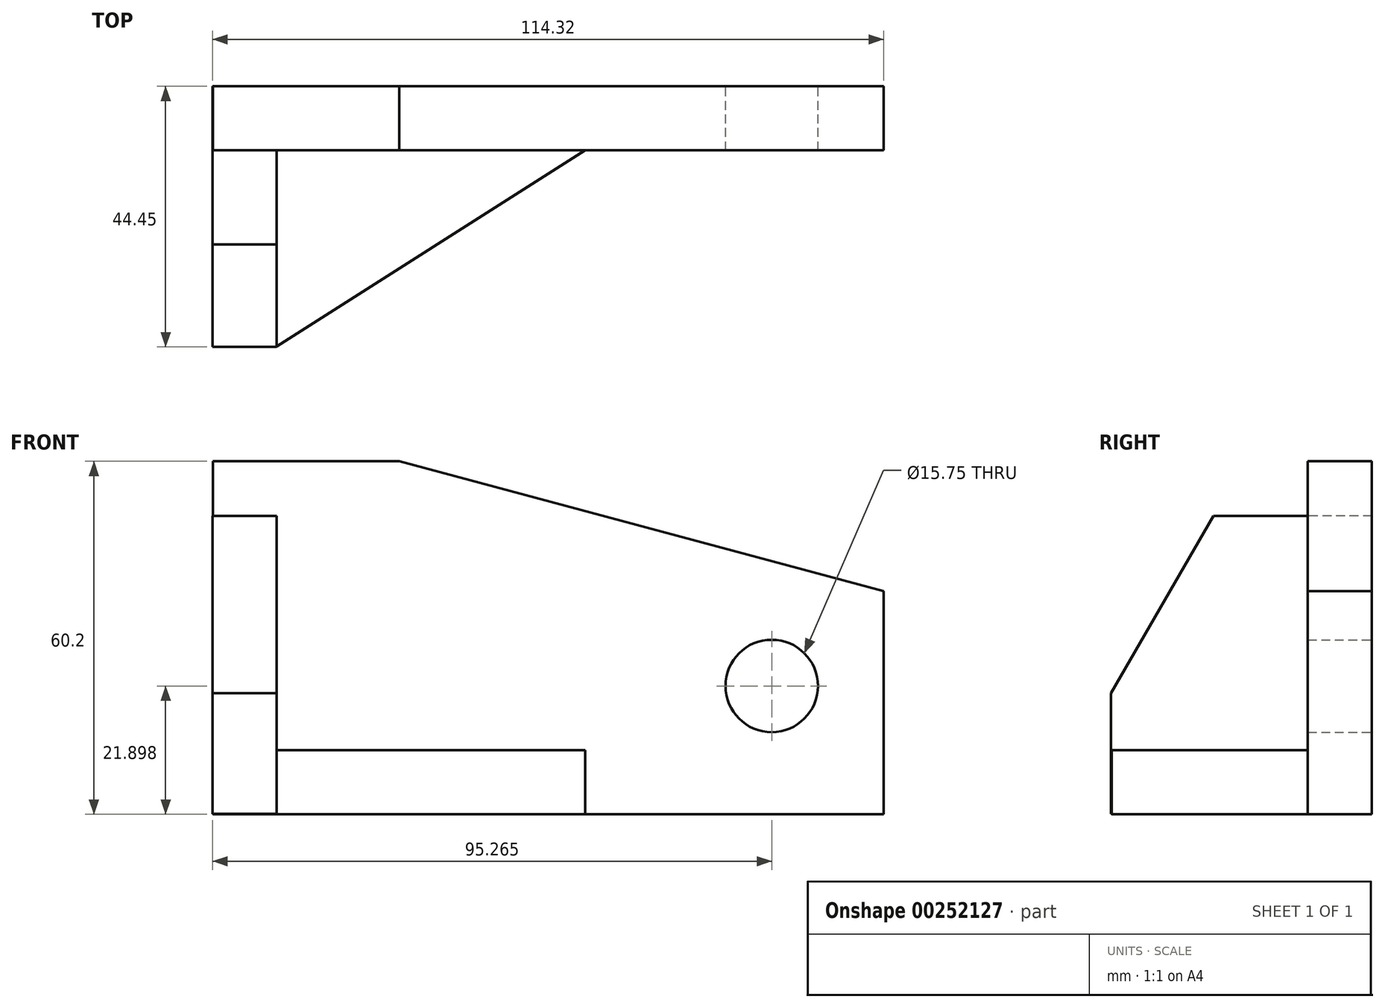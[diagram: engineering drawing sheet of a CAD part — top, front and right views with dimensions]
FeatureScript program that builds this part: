
annotation { "Feature Type Name" : "Feature", "Feature Type Description" : "" }
export const myFeature = defineFeature(function(context is Context, id is Id, definition is map)
    precondition{}
    {
        {
            var Q0;
            Q0=qCreatedBy(makeId("Front.planeOp"),FACE);
            var sketch = newSketch(context, id + "F0", { "sketchPlane" : qUnion([Q0])});
            skLineSegment(sketch, "E0", {"start": v(-57.08, 27.38) * mm, "end": v(-25.33, 27.38) * mm});
            skLineSegment(sketch, "E1", {"start": v(-57.08, 27.38) * mm, "end": v(-57.08, 0) * mm});
            skLineSegment(sketch, "E2", {"start": v(-57.08, 0) * mm, "end": v(-57.08, -32.82) * mm});
            skLineSegment(sketch, "E3", {"start": v(-57.08, -32.82) * mm, "end": v(0.07, -32.82) * mm});
            skLineSegment(sketch, "E4", {"start": v(0.07, -32.82) * mm, "end": v(57.22, -32.82) * mm});
            skLineSegment(sketch, "E5", {"start": v(-25.33, 27.38) * mm, "end": v(57.22, 5.26) * mm});
            skLineSegment(sketch, "E6", {"start": v(-25.33, 27.38) * mm, "end": v(57.22, 27.38) * mm, "construction": true});
            skLineSegment(sketch, "E7", {"start": v(57.22, -32.82) * mm, "end": v(57.22, 5.26) * mm});
            skCircle(sketch, "E8", {"center": v(38.17, -10.92) * mm, "radius": 7.87 * mm});
            skLineSegment(sketch, "E9", {"start": v(38.17, -10.92) * mm, "end": v(57.22, 5.26) * mm, "construction": true});
            skLineSegment(sketch, "E10", {"start": v(38.17, -10.92) * mm, "end": v(57.22, -32.82) * mm, "construction": true});
            skLineSegment(sketch, "E11", {"start": v(38.17, -10.92) * mm, "end": v(38.17, -32.82) * mm, "construction": true});
            skLineSegment(sketch, "E12", {"start": v(38.17, -10.92) * mm, "end": v(38.17, 10.37) * mm, "construction": true});
            skSolve(sketch);
        }
        {
            var Q0;
            Q0=makeQuery(id+"F0.imprint","IMPRINT",FACE,{"disambiguationData":[TD([[makeQuery(id+"F0.imprint","IMPRINT",EDGE,{"derivedFrom":sQuery(id+"F0.wireOp",EDGE,"E0")}),-1.0]])]});
            extrude(context, id + "F1", {"entities" : qUnion([Q0]), "depth" : 10.92 * mm});
        }
        {
            var Q0;
            Q0=qCreatedBy(makeId("Right.planeOp"),FACE);
            var sketch = newSketch(context, id + "F2", { "sketchPlane" : qUnion([Q0])});
            skLineSegment(sketch, "E13", {"start": v(0, -32.75) * mm, "end": v(-44.45, -32.75) * mm});
            skLineSegment(sketch, "E14", {"start": v(-44.45, -32.75) * mm, "end": v(-44.45, -12.17) * mm});
            skLineSegment(sketch, "E15", {"start": v(0, -32.75) * mm, "end": v(0, 18.05) * mm});
            skLineSegment(sketch, "E16", {"start": v(-44.45, -12.17) * mm, "end": v(-27, 18.05) * mm});
            skLineSegment(sketch, "E17", {"start": v(-44.45, -12.17) * mm, "end": v(-44.45, 32.56) * mm, "construction": true});
            skLineSegment(sketch, "E18", {"start": v(0, 18.05) * mm, "end": v(-27, 18.05) * mm});
            skSolve(sketch);
        }
        {
            var Q0;
            Q0=makeQuery(id+"F2.imprint","IMPRINT",FACE,{"disambiguationData":[TD([[makeQuery(id+"F2.imprint","IMPRINT",EDGE,{"derivedFrom":sQuery(id+"F2.wireOp",EDGE,"E13")}),-1.0]])]});
            extrude(context, id + "F3", {"entities" : qUnion([Q0]), "operationType" : NewBodyOperationType.ADD, "oppositeDirection" : true, "depth" : 57.1 * mm, "hasSecondDirection" : true, "secondDirectionOppositeDirection" : true, "secondDirectionDepth" : 46.18 * mm});
        }
        {
            var Q0;
            Q0=qCreatedBy(makeId("Top.planeOp"),FACE);
            var sketch = newSketch(context, id + "F4", { "sketchPlane" : qUnion([Q0])});
            skLineSegment(sketch, "E19", {"start": v(-46.17, -44.36) * mm, "end": v(-46.17, -10.91) * mm});
            skLineSegment(sketch, "E20", {"start": v(-46.17, -10.91) * mm, "end": v(6.4, -10.91) * mm});
            skLineSegment(sketch, "E21", {"start": v(-46.17, -44.36) * mm, "end": v(6.4, -10.91) * mm});
            skSolve(sketch);
        }
        {
            var Q0;
            Q0=makeQuery(id+"F4.imprint","IMPRINT",FACE,{"disambiguationData":[TD([[makeQuery(id+"F4.imprint","IMPRINT",EDGE,{"derivedFrom":sQuery(id+"F4.wireOp",EDGE,"E19")}),-1.0]])]});
            extrude(context, id + "F5", {"entities" : qUnion([Q0]), "operationType" : NewBodyOperationType.ADD, "oppositeDirection" : true, "depth" : 32.77 * mm, "hasSecondDirection" : true, "secondDirectionOppositeDirection" : true, "secondDirectionDepth" : 21.84 * mm});
        }
    });
